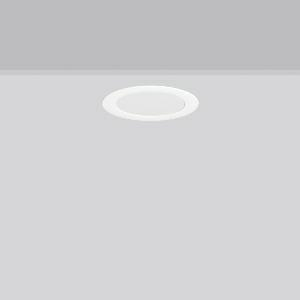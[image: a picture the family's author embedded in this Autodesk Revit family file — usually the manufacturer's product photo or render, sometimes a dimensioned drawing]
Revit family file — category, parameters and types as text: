
# Revit family: toledo_flat_round_e_672229_002_20fd
name_source: partatom
category: Lighting Fixtures
units: mm (PartAtom-declared; Revit-internal decimal feet)

## family parameters
Cut with Voids When Loaded = No
Host = Face
Light Source = No
Part Type = Normal
Room Calculation Point = No
Round Connector Dimension = Use Diameter
Shared = No

## types (1)
- TOLEDO FLAT round E (1 x LED Modul 830, 780 lm, 3000)
    Apparent Load = 8 VA
    CIE Flux Codes = 47 79 96 100 100
    Color Rendering = 80
    Color Temperature = 3000
    Default Elevation = 1800 mm
    Description = Series: TOLEDO FLAT round
Ultra thin recessed downlight. For escape route illumination. Housing: die-cast aluminium, powder-coated. Lightguide and diffuser made of non-yellowing plastic (PMMA). Diffuser opal matt plastic. Ceiling installation with spring system. Including separate LED converter with connecting cable 250 mm. Suitable for connection to central battery systems. External driver with simple plug-in locking system. 
Colour: white
Diameter: 190 mm
Height: 2.5 mm
Cut-out diameter: 170 mm
Recess height: 35 mm
Luminaire: recess height: 31-51 mm
Weight: 413 g
Operating mode: maintained power mode
Lamp: LED
Socket: without socket
Colour temperature: 3000K
Colour rendering index (CRI): 80
System power: 7.7 W
Rated luminous flux: 780 lm
Luminous flux, emergency: 780 lm
System power, emergency: 7.7 W
Control gear: Regulated power supply
Protection class: II
Type of protection: IP 54
    Height = 0 mm  [stored 0 ft]
    Lamp = 1 x LED Modul 830
    Lamp Light Flux = 780 lm
    Lamp count = 1
    Length = 190 mm  [stored 0.62336 ft]
    Lifetime = 50000 h
    Luminous efficacy = 101 lm/W
    Manufacturer = RZB
    ModVariant = No
    Model = 672229.002
    Mounting Place = Ceiling
    Mounting Type = Recessed
    Number of Poles = 1
    OnlyDefault = Yes
    Power Factor = 1
    Product Name = TOLEDO FLAT round E
    Product group = Recessed downlights
    ProductGroupID = 402
    Protection Class = Protection class II
    Protection Degree = IP 40
    RLX_Detail_Level = 1
    RLX_Emergency_Light_Flux = 780 lm
    RLX_Emergency_Type = 3
    RLX_Emergency_Type_DB = Yes
    RlxData = <blob elided: 29469 chars, md5=a7878fa5>
    Socket = socket
    Standby Power = 0 W
    System Light Flux = 780 lm
    System Power = 8 W
    Type Comments = Product without accessories
    Type Image = 901452.002.jpg
    URL = http://relux.com
    VarID = ---
    Voltage = 230 V
    Voltage Range = 220-240 V
    Weight = 0.00 kg
    Width = 0 mm  [stored 0 ft]

note: [stored X ft] marks values corroborated as IEEE doubles in the binary element streams (Revit-internal decimal feet)

## geometry (parser evidence)
native form markers: Blend x4, Sweep x10
no freeform markers — native parametric forms only
